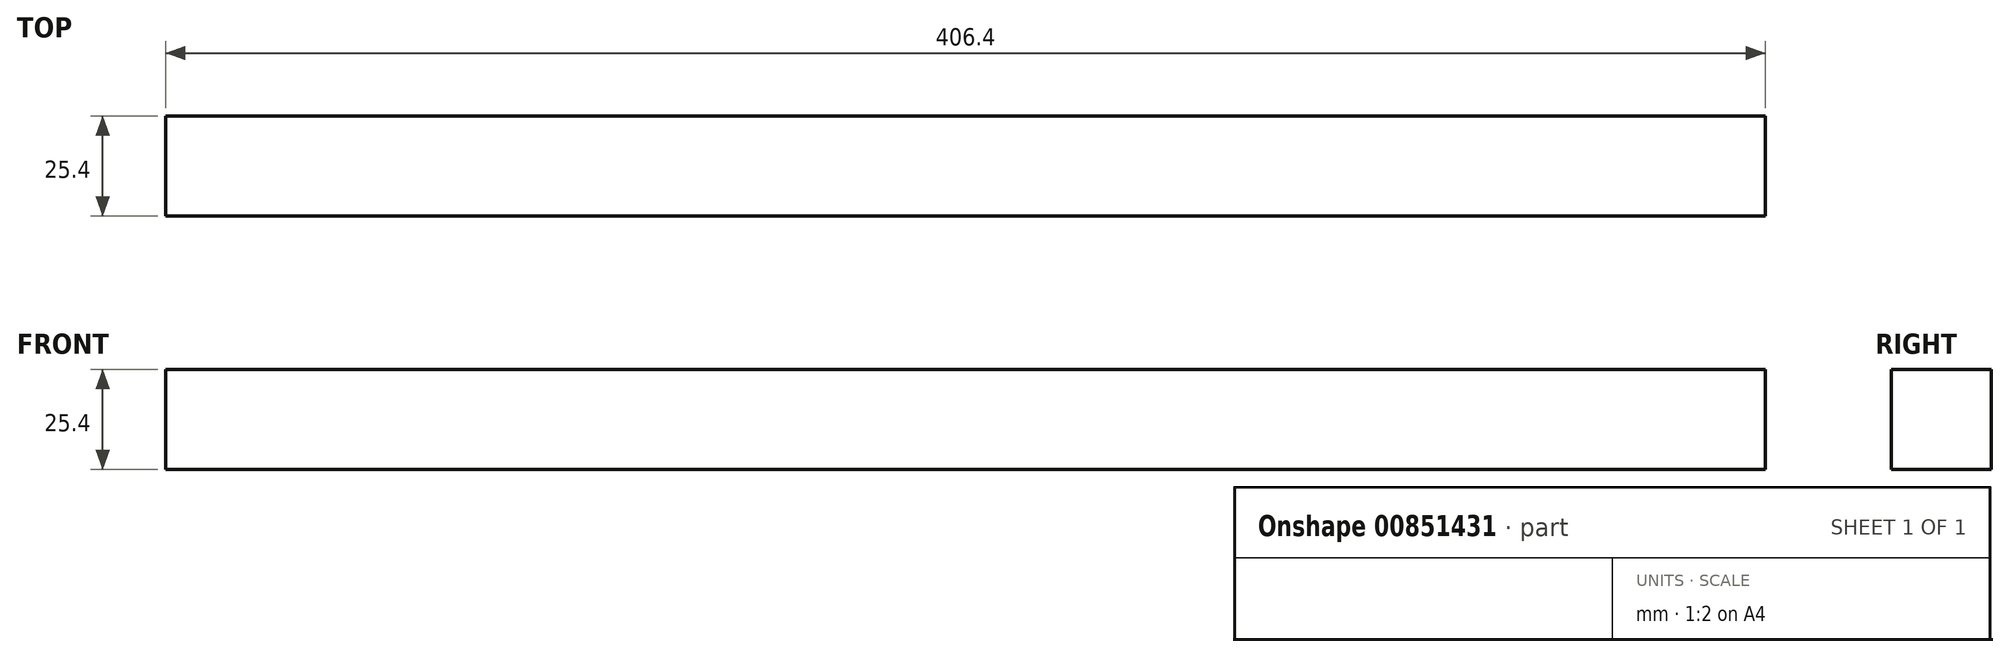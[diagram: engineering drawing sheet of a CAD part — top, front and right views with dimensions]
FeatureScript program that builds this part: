
annotation { "Feature Type Name" : "Feature", "Feature Type Description" : "" }
export const myFeature = defineFeature(function(context is Context, id is Id, definition is map)
    precondition{}
    {
        {
            var Q0;
            Q0=qCreatedBy(makeId("Front.planeOp"),FACE);
            var sketch = newSketch(context, id + "F0", { "sketchPlane" : qUnion([Q0])});
            skLineSegment(sketch, "E0.bottom", {"start": v(-34.97, 18.96) * mm, "end": v(371.43, 18.96) * mm});
            skLineSegment(sketch, "E0.top", {"start": v(-34.97, -6.44) * mm, "end": v(371.43, -6.44) * mm});
            skLineSegment(sketch, "E0.left", {"start": v(-34.97, 18.96) * mm, "end": v(-34.97, -6.44) * mm});
            skLineSegment(sketch, "E0.right", {"start": v(371.43, 18.96) * mm, "end": v(371.43, -6.44) * mm});
            skSolve(sketch);
        }
        {
            var Q0;
            Q0 = qSketchRegion(id + "F0", true);
            extrude(context, id + "F1", {"entities" : qUnion([Q0]), "depth" : 25.4 * mm, "offsetDistance" : 25 * mm});
        }
    });
